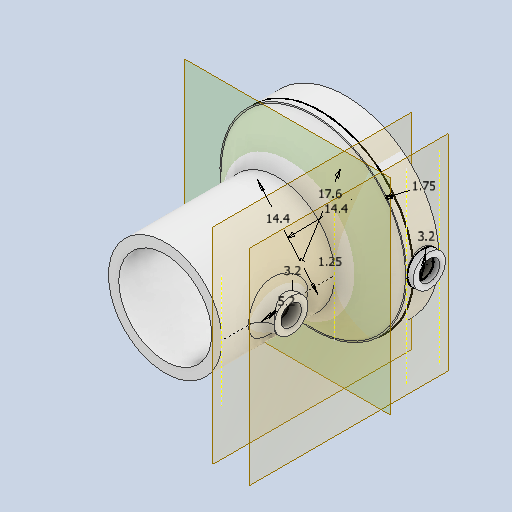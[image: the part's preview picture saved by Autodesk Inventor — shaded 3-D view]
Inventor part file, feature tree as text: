
AUTODESK INVENTOR PART (.ipt)
format: ipt  version: 2023 (Build 270158000, 158)  size: 395,264 bytes
history: native  units: in
note: dims shown in document units (in); Inventor stores cm internally (conversion verified against a paired STEP export)
features: extrude x11, sketch x5, plane x3, chamfer x2, fillet x1
ambient origin geometry x8: Origin, YZ Plane, XZ Plane, XY Plane, X Axis, Y Axis, Z Axis, Center Point
bodies: Solid1 (feature_tree)
feature tree (22):
  extrude  "Extrusion1"  Depth=1.1417in
  sketch  "Sketch2"  dims[d2=0.1575in d3=0.0in d4=0.5669in]
  extrude  "Extrusion2"  Depth=0.5669in
  extrude  "Extrusion3"  Depth=0.9449in TaperAngle=0.0deg
  chamfer  "Chamfer2"  Distance=0.0394in
  plane  "Work Plane1"
  sketch  "Sketch3"  dims[d5=0.6929in d6=0.9449in d7=0.0in d8=0.0394in d9=0.0in]
  extrude  "Extrusion4"  [1 undecoded]
  extrude  "Extrusion5"  Depth=0.0394in TaperAngle=0.0deg
  chamfer  "Chamfer3"  Distance=0.0394in
  plane  "Work Plane2"
  sketch  "Sketch4"  dims[d13=0.2165in d14=0.2559in d15=45.0deg d16=-0.3543in]
  extrude  "Extrusion6"  Depth=0.0492in TaperAngle=45.0deg
  extrude  "Extrusion7"  Depth=0.5669in
  plane  "Work Plane3"
  extrude  "Extrusion8"  Depth=0.126in
  sketch  "Sketch5"  dims[d17=0.0492in d18=0.0394in d19=0.0in d20=0.0394in d21=0.0in d22=0.0492in d23=0.0787in d24=45.0deg d25=0.5669in d26=0.126in d27=0.0394in d28=0.0in d29=0.0689in d30=0.0787in d31=0.0in d32=0.0197in d33=0.0in d34=0.126in d35=0.2047in d36=0.0787in d37=0.0in d38=0.0787in d39=0.0in d40=0.0197in d41=0.0in d42=0.0787in]
  extrude  "Extrusion9"  Depth=0.0394in TaperAngle=0.0deg
  extrude  "Extrusion10"  Depth=0.0689in
  extrude  "Extrusion11"  Depth=0.0787in TaperAngle=0.0deg
  fillet  "Fillet1"  Radius=0.0197in
  sketch  "Sketch1"  dims[d0=1.0039in d1=1.1417in]
note: 1 required parameter value undecoded (feature->parameter linkage not recoverable at this tier; creation-order binding heuristic only, values carry confidence <= 0.55)
